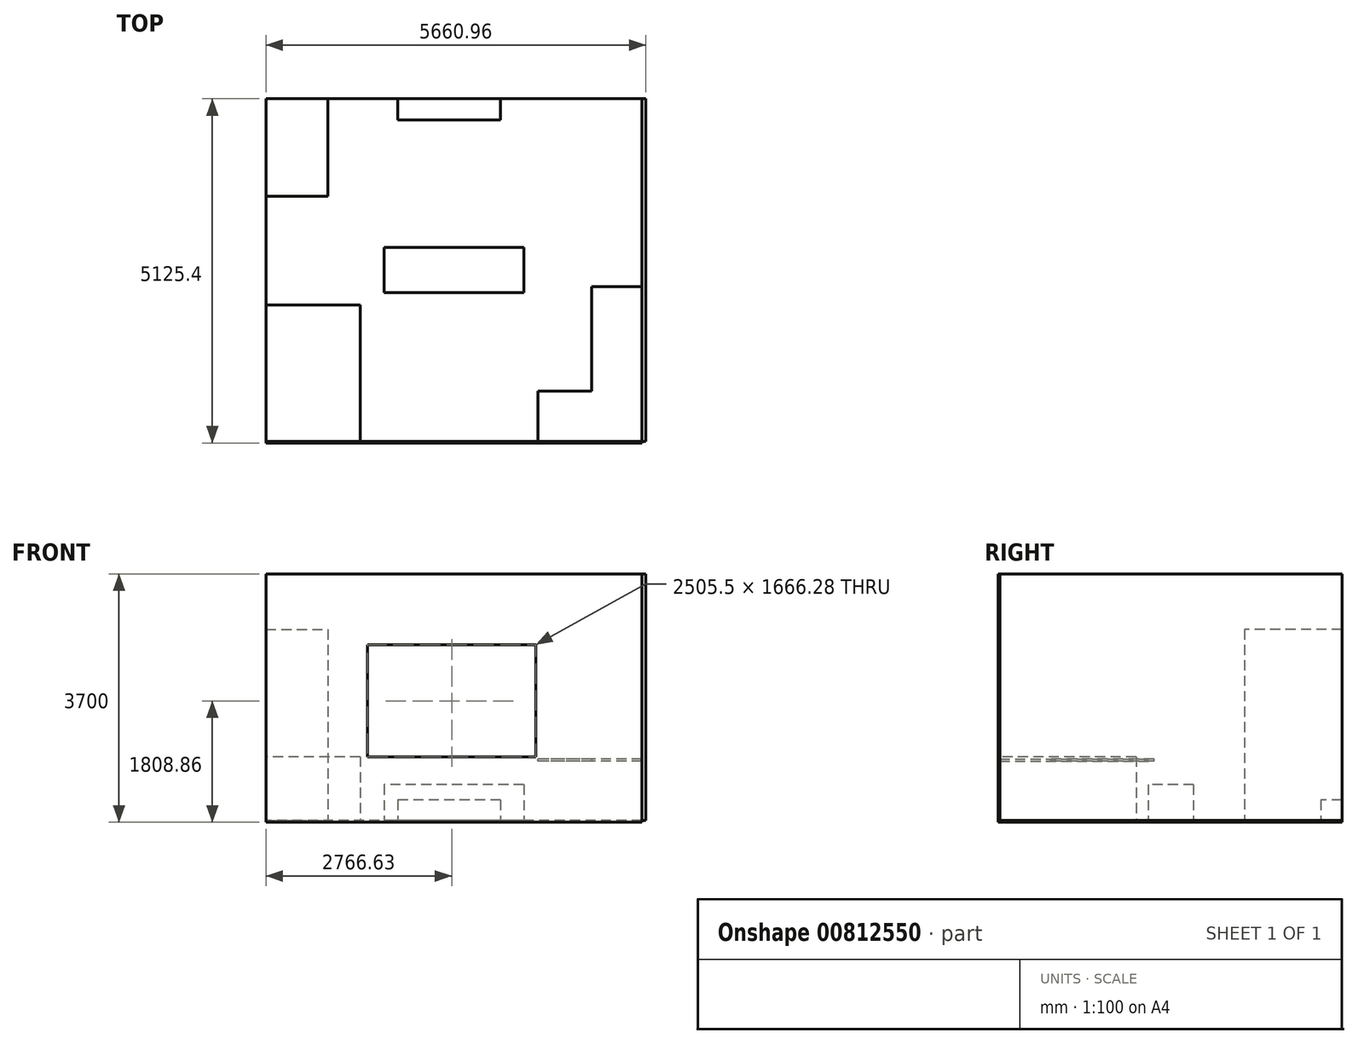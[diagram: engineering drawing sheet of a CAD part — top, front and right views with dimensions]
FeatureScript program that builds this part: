
annotation { "Feature Type Name" : "Feature", "Feature Type Description" : "" }
export const myFeature = defineFeature(function(context is Context, id is Id, definition is map)
    precondition{}
    {
        {
            var Q0;
            Q0=qCreatedBy(makeId("Top.planeOp"),FACE);
            var sketch = newSketch(context, id + "F0", { "sketchPlane" : qUnion([Q0])});
            skLineSegment(sketch, "E0.bottom", {"start": v(2800, 2550) * mm, "end": v(-2800, 2550) * mm});
            skLineSegment(sketch, "E0.top", {"start": v(2800, -2550) * mm, "end": v(-2800, -2550) * mm});
            skLineSegment(sketch, "E0.left", {"start": v(2800, 2550) * mm, "end": v(2800, -2550) * mm});
            skLineSegment(sketch, "E0.right", {"start": v(-2800, 2550) * mm, "end": v(-2800, -2550) * mm});
            skPoint(sketch, "E0.middle", {"position": v(0, 0) * mm});
            skSolve(sketch);
        }
        {
            var Q0;
            Q0 = qSketchRegion(id + "F0", true);
            var Q1;
            Q1=sQuery(id+"F0.wireOp",EDGE,"E0.top");
            extrude(context, id + "F1", {"entities" : qUnion([Q0]), "bodyType" : ToolBodyType.SURFACE, "surfaceEntities" : qUnion([Q1]), "depth" : 3700 * mm, "offsetDistance" : 25.4 * mm});
        }
        {
            var Q0;
            Q0 = qSketchRegion(id + "F0", true);
            extrude(context, id + "F2", {"entities" : qUnion([Q0]), "depth" : 25.4 * mm, "offsetDistance" : 25.4 * mm});
        }
        {
            var Q0;
            Q0=makeQuery(id+"F2.opExtrude","CAP_FACE",FACE,{"disambiguationData":[OSD([sQuery(id+"F0.wireOp",EDGE,"E0.bottom"),sQuery(id+"F0.wireOp",EDGE,"E0.top"),sQuery(id+"F0.wireOp",EDGE,"E0.left"),sQuery(id+"F0.wireOp",EDGE,"E0.right")])],"isStart":false});
            var sketch = newSketch(context, id + "F3", { "sketchPlane" : qUnion([Q0])});
            skLineSegment(sketch, "E1", {"start": v(2800, 2550) * mm, "end": v(2800, -2550) * mm});
            skSolve(sketch);
        }
        {
            var Q0;
            Q0 = qSketchRegion(id + "F3", true);
            var Q1;
            Q1 = qConstructionFilter(qBodyType(qCreatedBy(id + "F3" ,EDGE), BodyType.WIRE), ConstructionObject.NO);
            extrude(context, id + "F4", {"entities" : qUnion([Q0]), "bodyType" : ToolBodyType.SURFACE, "surfaceEntities" : qUnion([Q1]), "depth" : 3674.6 * mm, "offsetDistance" : 25.4 * mm});
        }
        {
            var Q0;
            Q0=makeQuery(id+"F1.opExtrude","SWEPT_FACE",FACE,{"disambiguationData":[OSD([sQuery(id+"F0.wireOp",EDGE,"E0.top")])]});
            var sketch = newSketch(context, id + "F5", { "sketchPlane" : qUnion([Q0])});
            skLineSegment(sketch, "E2", {"start": v(-2800, 0) * mm, "end": v(-2800, 940) * mm});
            skLineSegment(sketch, "E3", {"start": v(-2800, 940) * mm, "end": v(-1250, 940) * mm});
            skSolve(sketch);
        }
        {
            var Q0;
            Q0=sQuery(id+"F5.wireOp",EDGE,"E3");
            extrude(context, id + "F6", {"bodyType" : ToolBodyType.SURFACE, "surfaceEntities" : qUnion([Q0]), "depth" : 750 * mm, "offsetDistance" : 25.4 * mm});
        }
        {
            var Q0;
            Q0=makeQuery(id+"F6.opExtrude","SWEPT_FACE",FACE,{"disambiguationData":[OSD([sQuery(id+"F5.wireOp",EDGE,"E3")])]});
            extrude(context, id + "F7", {"entities" : qUnion([Q0]), "depth" : 30 * mm, "offsetDistance" : 25.4 * mm});
        }
        {
            var Q0;
            {var subQ0=sQuery(id+"F5.wireOp",EDGE,"E3");Q0=makeQuery(id+"F7.opExtrude","SWEPT_FACE",FACE,{"disambiguationData":[OSD([subQ0]),TDD([makeQuery(id+"F6.opExtrude","CAP_EDGE",EDGE,{"disambiguationData":[OSD([subQ0])],"isStart":false})])]});}
            var sketch = newSketch(context, id + "F8", { "sketchPlane" : qUnion([Q0])});
            skLineSegment(sketch, "E4.bottom", {"start": v(-2800, 940) * mm, "end": v(-2050, 940) * mm});
            skLineSegment(sketch, "E4.top", {"start": v(-2800, 910) * mm, "end": v(-2050, 910) * mm});
            skLineSegment(sketch, "E4.left", {"start": v(-2800, 940) * mm, "end": v(-2800, 910) * mm});
            skLineSegment(sketch, "E4.right", {"start": v(-2050, 940) * mm, "end": v(-2050, 910) * mm});
            skSolve(sketch);
        }
        {
            var Q0;
            Q0 = qSketchRegion(id + "F8", true);
            extrude(context, id + "F9", {"entities" : qUnion([Q0]), "operationType" : NewBodyOperationType.ADD, "depth" : 1550 * mm, "offsetDistance" : 25.4 * mm});
        }
        {
            var Q0;
            Q0=makeQuery(id+"F1.opExtrude","SWEPT_FACE",FACE,{"disambiguationData":[OSD([sQuery(id+"F0.wireOp",EDGE,"E0.top")])]});
            extrude(context, id + "F10", {"entities" : qUnion([Q0]), "oppositeDirection" : true, "depth" : 25.4 * mm, "offsetDistance" : 25.4 * mm});
        }
        {
            var Q0;
            Q0=makeQuery(id+"F4.opExtrude","SWEPT_FACE",FACE,{"disambiguationData":[OSD([sQuery(id+"F3.wireOp",EDGE,"E1")])]});
            extrude(context, id + "F11", {"entities" : qUnion([Q0]), "oppositeDirection" : true, "depth" : 60.96 * mm, "offsetDistance" : 25.4 * mm});
        }
        {
            var Q0;
            Q0=makeQuery(id+"F10.opExtrude","CAP_FACE",FACE,{"disambiguationData":[OSD([sQuery(id+"F0.wireOp",EDGE,"E0.top")])],"isStart":true});
            var sketch = newSketch(context, id + "F12", { "sketchPlane" : qUnion([Q0])});
            skLineSegment(sketch, "E5.bottom", {"start": v(-1219.37, 975.72) * mm, "end": v(1286.12, 975.72) * mm});
            skLineSegment(sketch, "E5.top", {"start": v(-1219.37, 2642) * mm, "end": v(1286.12, 2642) * mm});
            skLineSegment(sketch, "E5.left", {"start": v(-1219.37, 975.72) * mm, "end": v(-1219.37, 2642) * mm});
            skLineSegment(sketch, "E5.right", {"start": v(1286.12, 975.72) * mm, "end": v(1286.12, 2642) * mm});
            skSolve(sketch);
        }
        {
            var Q0;
            Q0 = qSketchRegion(id + "F12", true);
            extrude(context, id + "F13", {"entities" : qUnion([Q0]), "operationType" : NewBodyOperationType.REMOVE, "oppositeDirection" : true, "depth" : 330.2 * mm, "offsetDistance" : 25.4 * mm});
        }
        {
            var Q0;
            Q0=makeQuery(id+"F10.opExtrude","CAP_FACE",FACE,{"disambiguationData":[OSD([sQuery(id+"F0.wireOp",EDGE,"E0.top")])],"isStart":true});
            var sketch = newSketch(context, id + "F14", { "sketchPlane" : qUnion([Q0])});
            skLineSegment(sketch, "E6.bottom", {"start": v(1395.59, 975.72) * mm, "end": v(2800, 975.72) * mm});
            skLineSegment(sketch, "E6.top", {"start": v(1395.59, 0) * mm, "end": v(2800, 0) * mm});
            skLineSegment(sketch, "E6.left", {"start": v(1395.59, 975.72) * mm, "end": v(1395.59, 0) * mm});
            skLineSegment(sketch, "E6.right", {"start": v(2800, 975.72) * mm, "end": v(2800, 0) * mm});
            skSolve(sketch);
        }
        {
            var Q0;
            Q0 = qSketchRegion(id + "F14", true);
            extrude(context, id + "F15", {"entities" : qUnion([Q0]), "depth" : 2032 * mm, "offsetDistance" : 25.4 * mm});
        }
        {
            var Q0;
            Q0=makeQuery(id+"F2.opExtrude","CAP_FACE",FACE,{"disambiguationData":[OSD([sQuery(id+"F0.wireOp",EDGE,"E0.bottom"),sQuery(id+"F0.wireOp",EDGE,"E0.top"),sQuery(id+"F0.wireOp",EDGE,"E0.left"),sQuery(id+"F0.wireOp",EDGE,"E0.right")])],"isStart":false});
            var sketch = newSketch(context, id + "F16", { "sketchPlane" : qUnion([Q0])});
            skLineSegment(sketch, "E7.bottom", {"start": v(-2800, 2550) * mm, "end": v(-1880.34, 2550) * mm});
            skLineSegment(sketch, "E7.top", {"start": v(-2800, 1097.48) * mm, "end": v(-1880.34, 1097.48) * mm});
            skLineSegment(sketch, "E7.left", {"start": v(-2800, 2550) * mm, "end": v(-2800, 1097.48) * mm});
            skLineSegment(sketch, "E7.right", {"start": v(-1880.34, 2550) * mm, "end": v(-1880.34, 1097.48) * mm});
            skSolve(sketch);
        }
        {
            var Q0;
            Q0 = qSketchRegion(id + "F16", true);
            extrude(context, id + "F17", {"entities" : qUnion([Q0]), "depth" : 2847.34 * mm, "offsetDistance" : 25.4 * mm});
        }
        {
            var Q0;
            Q0=makeQuery(id+"F2.opExtrude","CAP_FACE",FACE,{"disambiguationData":[OSD([sQuery(id+"F0.wireOp",EDGE,"E0.bottom"),sQuery(id+"F0.wireOp",EDGE,"E0.top"),sQuery(id+"F0.wireOp",EDGE,"E0.left"),sQuery(id+"F0.wireOp",EDGE,"E0.right")])],"isStart":false});
            var sketch = newSketch(context, id + "F18", { "sketchPlane" : qUnion([Q0])});
            skLineSegment(sketch, "E8.bottom", {"start": v(1041.6, 338.1) * mm, "end": v(-1041.6, 338.1) * mm});
            skLineSegment(sketch, "E8.top", {"start": v(1041.6, -338.1) * mm, "end": v(-1041.6, -338.1) * mm});
            skLineSegment(sketch, "E8.left", {"start": v(1041.6, 338.1) * mm, "end": v(1041.6, -338.1) * mm});
            skLineSegment(sketch, "E8.right", {"start": v(-1041.6, 338.1) * mm, "end": v(-1041.6, -338.1) * mm});
            skPoint(sketch, "E8.middle", {"position": v(0, 0) * mm});
            skSolve(sketch);
        }
        {
            var Q0;
            Q0 = qSketchRegion(id + "F18", true);
            extrude(context, id + "F19", {"entities" : qUnion([Q0]), "depth" : 533.4 * mm, "offsetDistance" : 25.4 * mm});
        }
        {
            var Q0;
            Q0=makeQuery(id+"F2.opExtrude","CAP_FACE",FACE,{"disambiguationData":[OSD([sQuery(id+"F0.wireOp",EDGE,"E0.bottom"),sQuery(id+"F0.wireOp",EDGE,"E0.top"),sQuery(id+"F0.wireOp",EDGE,"E0.left"),sQuery(id+"F0.wireOp",EDGE,"E0.right")])],"isStart":false});
            var sketch = newSketch(context, id + "F20", { "sketchPlane" : qUnion([Q0])});
            skLineSegment(sketch, "E9.bottom", {"start": v(-840.33, 2550) * mm, "end": v(694.93, 2550) * mm});
            skLineSegment(sketch, "E9.top", {"start": v(-840.33, 2236.54) * mm, "end": v(694.93, 2236.54) * mm});
            skLineSegment(sketch, "E9.left", {"start": v(-840.33, 2550) * mm, "end": v(-840.33, 2236.54) * mm});
            skLineSegment(sketch, "E9.right", {"start": v(694.93, 2550) * mm, "end": v(694.93, 2236.54) * mm});
            skSolve(sketch);
        }
        {
            var Q0;
            Q0 = qSketchRegion(id + "F20", true);
            extrude(context, id + "F21", {"entities" : qUnion([Q0]), "depth" : 304.8 * mm, "offsetDistance" : 25.4 * mm});
        }
    });
